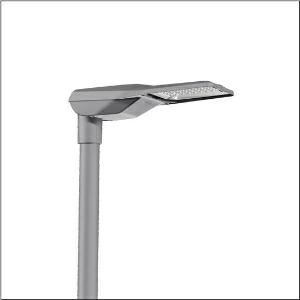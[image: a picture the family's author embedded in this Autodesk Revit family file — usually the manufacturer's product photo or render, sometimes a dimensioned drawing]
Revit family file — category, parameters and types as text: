
# Revit family: streetlight_sl_21_mini___st1_0ab_5xe6m33a08hb_b9bd
name_source: partatom
category: Lighting Fixtures
units: mm (PartAtom-declared; Revit-internal decimal feet)

## family parameters
Cut with Voids When Loaded = No
Host = Face
Light Source = No
Part Type = Normal
Room Calculation Point = No
Round Connector Dimension = Use Diameter
Shared = No

## types (1)
- --- (1 x LED, 7960 lm, 66 W, 3000K)
    Apparent Load = 66 VA
    CIE Flux Codes = 38 73 97 100 100
    Color Rendering = 70
    Color Temperature = 3000K
    Default Elevation = 1800 mm
    Description = Streetlight SL 21 mini, mast luminaire, primary light control with lens, of PMMA, primary optical cover: cover, of toughened safety glass, transparent, light distribution: ST1.0aB, light emission: direct distribution, primary light characteristic: asymmetric, installation type: post-top, side-entry, LED, 3G 1.5mm², High Power LED, rated luminous flux: 7.960lm, luminous efficacy: 121lm/W, light colour: 730, colour temperature: 3000K, control: flexible luminous flux parameterisation, time-dependent luminous flux control, constant luminous flux control, overheat protection, mains connection: 230..240V, AC, 50/60Hz, connection cable pre-assembled, cable length: 8,5m, wiring characteristics: H07RN-F, start of lifetime: 66W, end of service life: 69W, reduction: 30W, luminaire housing, of diecast aluminium, powder-coated, Siteco® metallic grey (DB 702S), corrosivity category C5 mid according to DIN EN ISO 12944, please order mast flange separately, inclination adjustable: 0°, 5°, 10°, 15°, sealing non-destructively replaceable, multi-level sealing system, length: 628mm, width: 235mm, height: 110mm, mast flange for spigot size: 42mm (side-entry): 5XC10008XM4, 60/48mm (side-entry/post-top): 5XC10108XM2, 76/60mm (side-entry/post-top): 5XC10108XM1, protection rating (complete): IP66, insulation class (complete): insulation class II (safety insulation), certification: CE, ENEC, ENEC+, VDE, impact resistance: IK09, permissible operating ambient temperature for outdoor applications: -40..+50°C, standard-compliant lighting for roads and squares, packaging unit: 1 piece

Light Distribution: ST1.0aB
    Height = 110 mm
    Lamp = 1 x LED
    Lamp Light Flux = 7960 lm
    Lamp Power = 66 W
    Lamp count = 1
    Length = 625 mm
    Luminous efficacy = 121 lm/W
    Manufacturer = Siteco
    ModVariant = No
    Model = 5XE6M33A08HB
    Number of Poles = 1
    OnlyDefault = Yes
    Power Factor = 1
    Product Name = Streetlight SL 21 mini | ST1.0aB
    Product group = mast luminaire | pylon top
    ProductGroupID = 6100
    Protection Class = Protection class II
    Protection Degree = IP 66
    RLX_Detail_Level = 1
    RLX_Emergency_Light_Flux = 0 lm
    RLX_Emergency_Type = 0
    RLX_Emergency_Type_DB = No
    RlxData = <blob elided: 92153 chars, md5=ad57929d>
    Socket = socket
    Standby Power = 0 W
    System Light Flux = 7960 lm
    System Power = 66 W
    Type Comments = factory setting: luminous flux: 100 % | Output Level: 100 % | 670 mA
    Type Image = l_1003519.jpg
    URL = http://relux.com
    VarID = @adj_133879
    Voltage = 0 V
    Weight = 0.00 kg
    Width = 234 mm

## geometry (parser evidence)
native form markers: Blend x4, Sweep x12
no freeform markers — native parametric forms only
